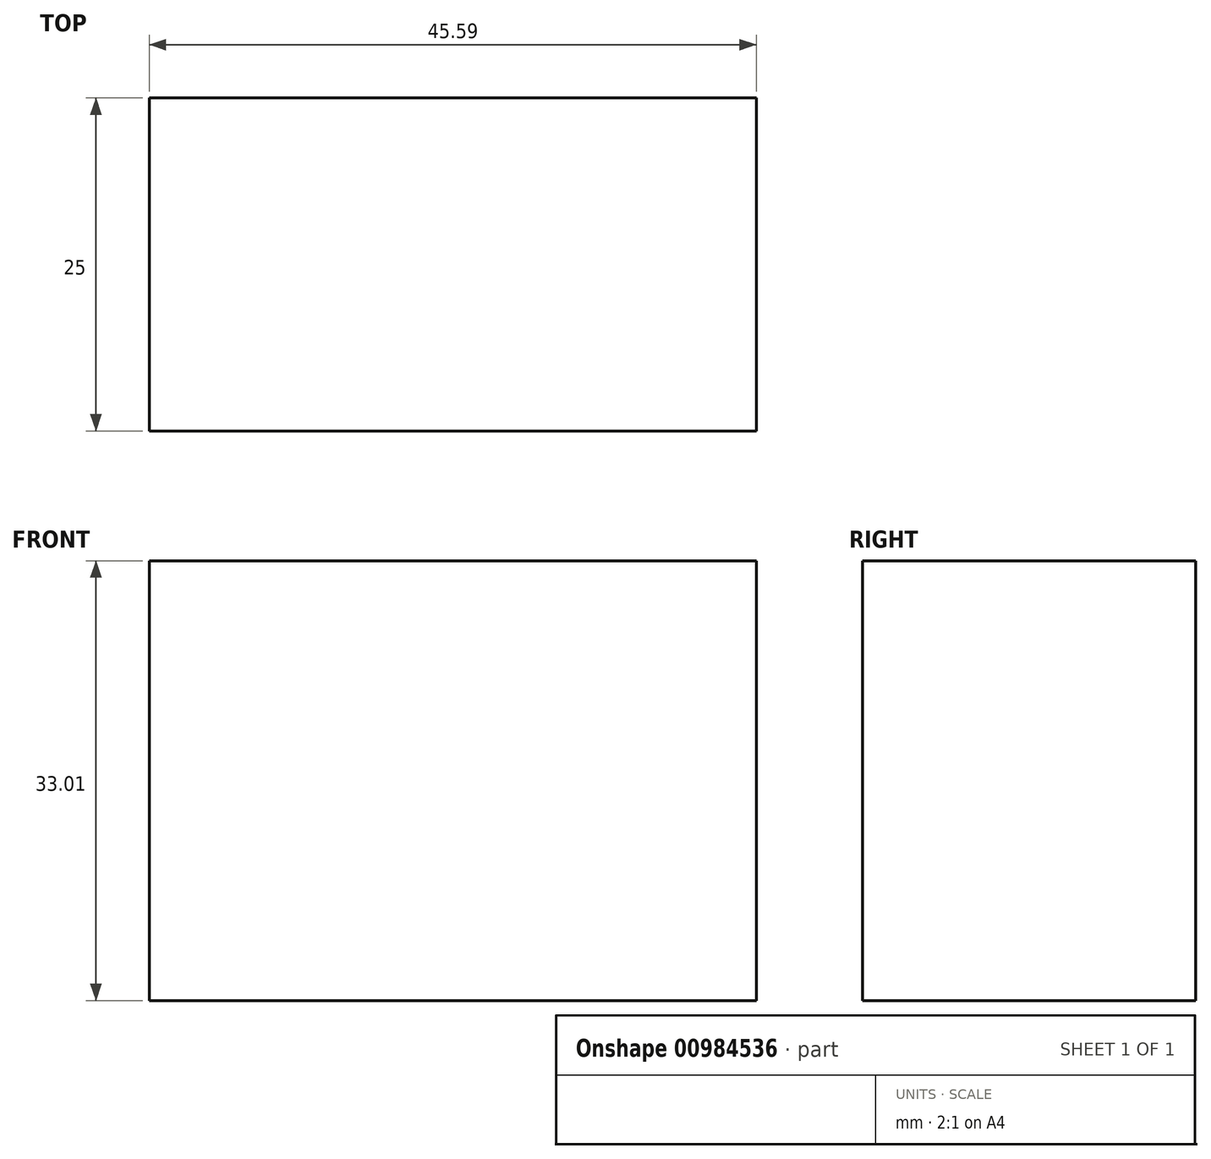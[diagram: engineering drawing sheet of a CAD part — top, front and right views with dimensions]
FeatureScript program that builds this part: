
annotation { "Feature Type Name" : "Feature", "Feature Type Description" : "" }
export const myFeature = defineFeature(function(context is Context, id is Id, definition is map)
    precondition{}
    {
        {
            var Q0;
            Q0=qCreatedBy(makeId("Front.planeOp"),FACE);
            var sketch = newSketch(context, id + "F0", { "sketchPlane" : qUnion([Q0])});
            skLineSegment(sketch, "E0.bottom", {"start": v(-110.76, 27.79) * mm, "end": v(-65.17, 27.79) * mm});
            skLineSegment(sketch, "E0.top", {"start": v(-110.76, -5.22) * mm, "end": v(-65.17, -5.22) * mm});
            skLineSegment(sketch, "E0.left", {"start": v(-110.76, 27.79) * mm, "end": v(-110.76, -5.22) * mm});
            skLineSegment(sketch, "E0.right", {"start": v(-65.17, 27.79) * mm, "end": v(-65.17, -5.22) * mm});
            skSolve(sketch);
        }
        {
            var Q0;
            Q0 = qSketchRegion(id + "F0", true);
            extrude(context, id + "F1", {"entities" : qUnion([Q0]), "depth" : 25 * mm, "offsetDistance" : 25 * mm});
        }
    });
